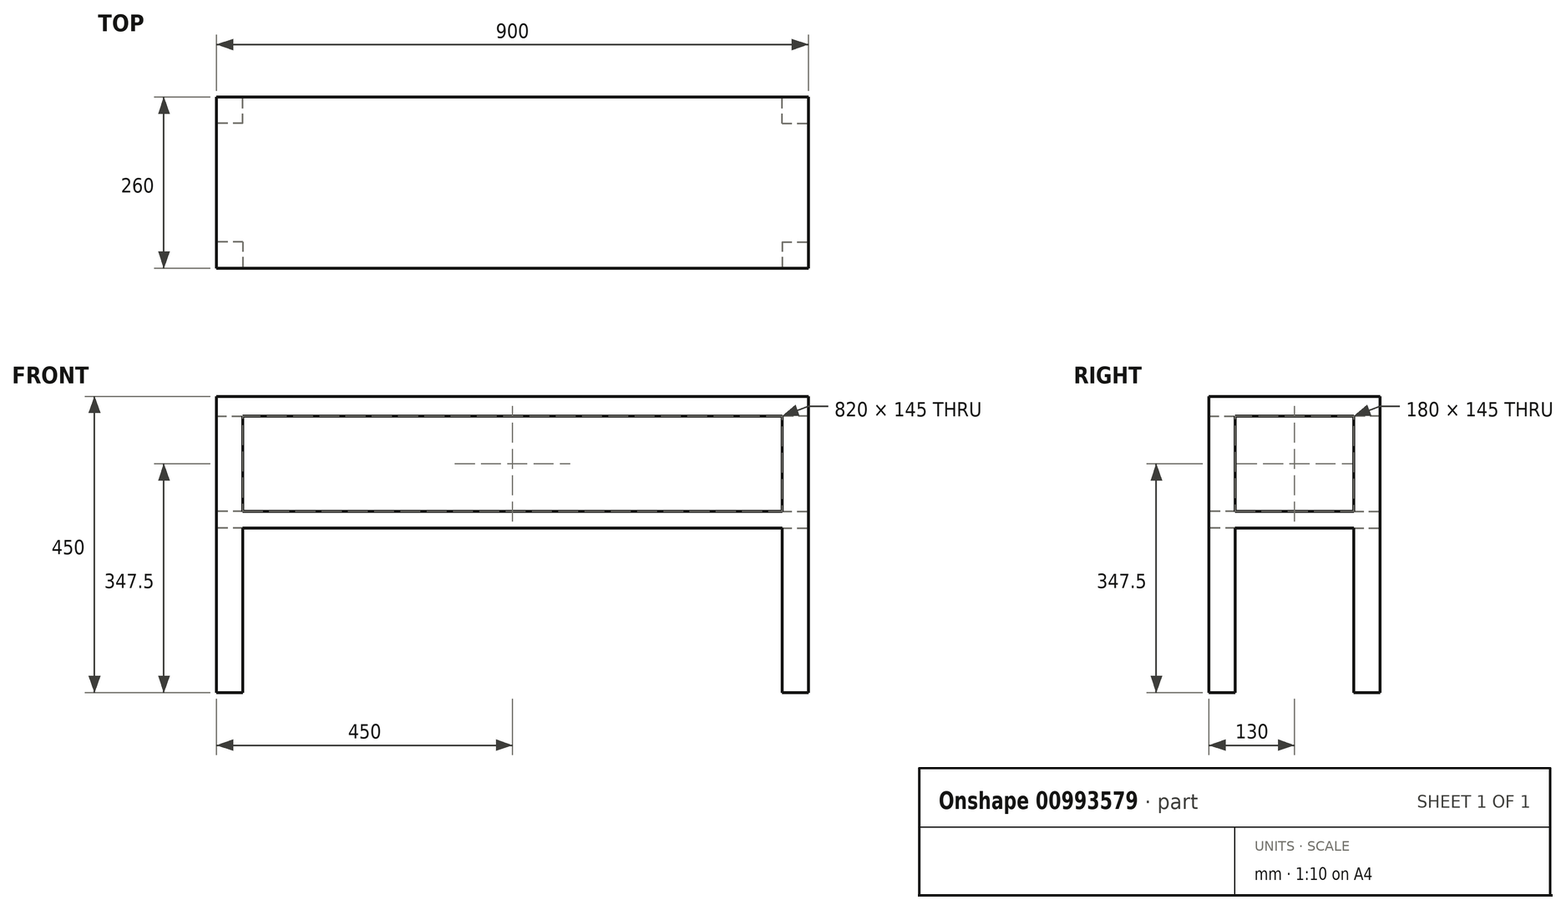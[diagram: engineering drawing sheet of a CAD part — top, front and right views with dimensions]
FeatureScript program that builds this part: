
annotation { "Feature Type Name" : "Feature", "Feature Type Description" : "" }
export const myFeature = defineFeature(function(context is Context, id is Id, definition is map)
    precondition{}
    {
        {
            var Q0;
            Q0=qCreatedBy(makeId("Top.planeOp"),FACE);
            var sketch = newSketch(context, id + "F0", { "sketchPlane" : qUnion([Q0])});
            skLineSegment(sketch, "E0.bottom", {"start": v(450, 130) * mm, "end": v(-450, 130) * mm});
            skLineSegment(sketch, "E0.top", {"start": v(450, -130) * mm, "end": v(-450, -130) * mm});
            skLineSegment(sketch, "E0.left", {"start": v(450, 130) * mm, "end": v(450, -130) * mm});
            skLineSegment(sketch, "E0.right", {"start": v(-450, 130) * mm, "end": v(-450, -130) * mm});
            skPoint(sketch, "E0.middle", {"position": v(0, 0) * mm});
            skSolve(sketch);
        }
        {
            var Q0;
            Q0 = qSketchRegion(id + "F0", true);
            extrude(context, id + "F1", {"entities" : qUnion([Q0]), "oppositeDirection" : true, "depth" : 30 * mm, "offsetDistance" : 25 * mm});
        }
        {
            var Q0;
            Q0=qCreatedBy(makeId("Top.planeOp"),FACE);
            var sketch = newSketch(context, id + "F2", { "sketchPlane" : qUnion([Q0])});
            skLineSegment(sketch, "E1.bottom", {"start": v(450, 130) * mm, "end": v(410, 130) * mm});
            skLineSegment(sketch, "E1.top", {"start": v(450, 90) * mm, "end": v(410, 90) * mm});
            skLineSegment(sketch, "E1.left", {"start": v(450, 130) * mm, "end": v(450, 90) * mm});
            skLineSegment(sketch, "E1.right", {"start": v(410, 130) * mm, "end": v(410, 90) * mm});
            skPoint(sketch, "E1.middle", {"position": v(430, 110) * mm});
            skLineSegment(sketch, "E2.MirrorCS", {"start": v(-450, 90) * mm, "end": v(-410, 90) * mm});
            skLineSegment(sketch, "E3.MirrorCS", {"start": v(-410, 130) * mm, "end": v(-410, 90) * mm});
            skPoint(sketch, "E4.MirrorP", {"position": v(-430, 110) * mm});
            skLineSegment(sketch, "E5.MirrorCS", {"start": v(-450, 130) * mm, "end": v(-410, 130) * mm});
            skLineSegment(sketch, "E6.MirrorCS", {"start": v(-450, 130) * mm, "end": v(-450, 90) * mm});
            skPoint(sketch, "E7.MirrorP", {"position": v(-430, -110) * mm});
            skLineSegment(sketch, "E8.MirrorCS", {"start": v(-410, -130) * mm, "end": v(-410, -90) * mm});
            skLineSegment(sketch, "E9.MirrorCS", {"start": v(-450, -130) * mm, "end": v(-450, -90) * mm});
            skLineSegment(sketch, "E10.MirrorCS", {"start": v(-450, -130) * mm, "end": v(-410, -130) * mm});
            skLineSegment(sketch, "E11.MirrorCS", {"start": v(-450, -90) * mm, "end": v(-410, -90) * mm});
            skPoint(sketch, "E12.MirrorP", {"position": v(430, -110) * mm});
            skLineSegment(sketch, "E13.MirrorCS", {"start": v(450, -130) * mm, "end": v(410, -130) * mm});
            skLineSegment(sketch, "E14.MirrorCS", {"start": v(410, -130) * mm, "end": v(410, -90) * mm});
            skLineSegment(sketch, "E15.MirrorCS", {"start": v(450, -130) * mm, "end": v(450, -90) * mm});
            skLineSegment(sketch, "E16.MirrorCS", {"start": v(450, -90) * mm, "end": v(410, -90) * mm});
            skSolve(sketch);
        }
        {
            var Q0;
            Q0 = qSketchRegion(id + "F2", true);
            extrude(context, id + "F3", {"entities" : qUnion([Q0]), "operationType" : NewBodyOperationType.ADD, "oppositeDirection" : true, "depth" : 450 * mm, "offsetDistance" : 25 * mm});
        }
        {
            var Q0;
            Q0=qCreatedBy(makeId("Top.planeOp"),FACE);
            cPlane(context, id + "F4", {"entities" : qUnion([Q0]), "cplaneType" : CPlaneType.OFFSET, "offset" : 200 * mm, "oppositeDirection" : true, "width" : 150 * mm, "height" : 150 * mm});
        }
        {
            var Q0;
            Q0=qCreatedBy(id+"F4.planeOp",FACE);
            var sketch = newSketch(context, id + "F5", { "sketchPlane" : qUnion([Q0])});
            skLineSegment(sketch, "E17.0", {"start": v(450, 130) * mm, "end": v(-450, 130) * mm});
            skLineSegment(sketch, "E17.1", {"start": v(450, -130) * mm, "end": v(-450, -130) * mm});
            skLineSegment(sketch, "E17.2", {"start": v(450, 130) * mm, "end": v(450, -130) * mm});
            skLineSegment(sketch, "E17.3", {"start": v(-450, 130) * mm, "end": v(-450, -130) * mm});
            skPoint(sketch, "E17.4", {"position": v(0, 0) * mm});
            skSolve(sketch);
        }
        {
            var Q0;
            Q0 = qSketchRegion(id + "F5", true);
            extrude(context, id + "F6", {"entities" : qUnion([Q0]), "operationType" : NewBodyOperationType.ADD, "depth" : 25 * mm, "offsetDistance" : 25 * mm});
        }
    });
